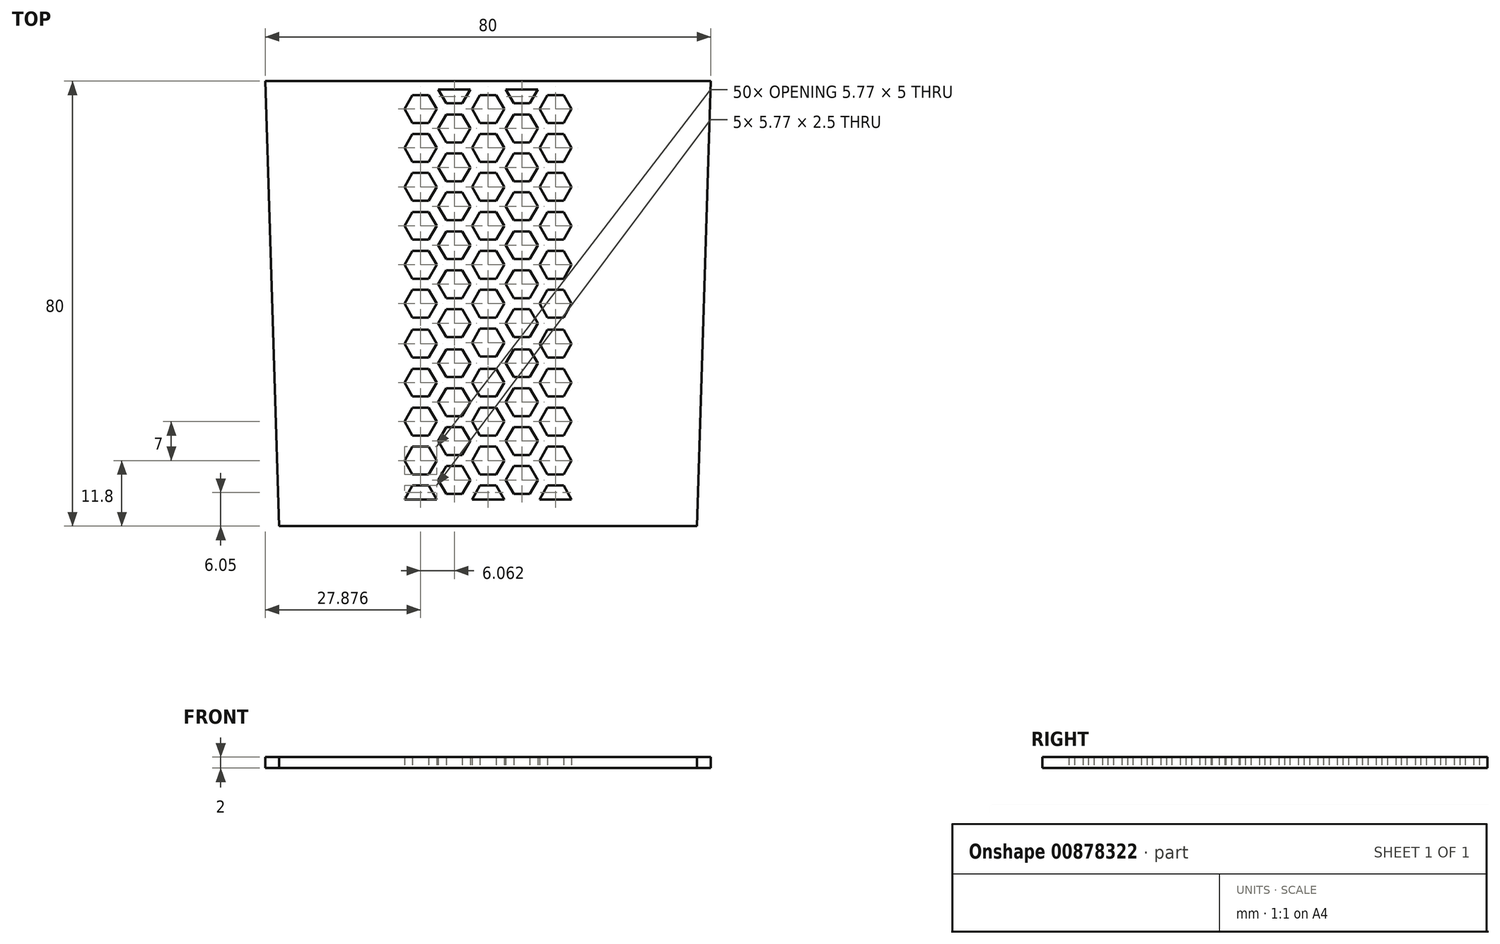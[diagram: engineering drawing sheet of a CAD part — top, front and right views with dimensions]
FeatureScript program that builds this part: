
annotation { "Feature Type Name" : "Feature", "Feature Type Description" : "" }
export const myFeature = defineFeature(function(context is Context, id is Id, definition is map)
    precondition{}
    {
        {
            var Q0;
            Q0=qCreatedBy(makeId("Top.planeOp"),FACE);
            var sketch = newSketch(context, id + "F0", { "sketchPlane" : qUnion([Q0])});
            skLineSegment(sketch, "E0.bottom", {"start": v(37.5, -40) * mm, "end": v(-37.5, -40) * mm});
            skLineSegment(sketch, "E0.top", {"start": v(40, 40) * mm, "end": v(-40, 40) * mm});
            skLineSegment(sketch, "E1", {"start": v(-40, 40) * mm, "end": v(-37.5, -40) * mm});
            skLineSegment(sketch, "E2", {"start": v(40, 40) * mm, "end": v(37.5, -40) * mm});
            skPoint(sketch, "E3.orphan", {"position": v(-40, -40) * mm});
            skPoint(sketch, "E4.orphan", {"position": v(40, -40) * mm});
            skCircle(sketch, "E5.cCircle", {"center": v(0, 0) * mm, "radius": 2.5 * mm, "construction": true});
            skLineSegment(sketch, "E5.0", {"start": v(1.44, -2.5) * mm, "end": v(-1.44, -2.5) * mm});
            skLineSegment(sketch, "E5.1", {"start": v(-1.44, -2.5) * mm, "end": v(-2.89, 0) * mm});
            skLineSegment(sketch, "E5.2", {"start": v(-2.89, 0) * mm, "end": v(-1.44, 2.5) * mm});
            skLineSegment(sketch, "E5.3", {"start": v(-1.44, 2.5) * mm, "end": v(1.44, 2.5) * mm});
            skLineSegment(sketch, "E5.4", {"start": v(1.44, 2.5) * mm, "end": v(2.89, 0) * mm});
            skLineSegment(sketch, "E5.5", {"start": v(2.89, 0) * mm, "end": v(1.44, -2.5) * mm});
            skPoint(sketch, "E5.0.midPoint", {"position": v(0, -2.5) * mm});
            skCircle(sketch, "E6.cCircle", {"center": v(6.06, -3.5) * mm, "radius": 2.5 * mm, "construction": true});
            skLineSegment(sketch, "E6.0", {"start": v(7.5, -6) * mm, "end": v(4.62, -6) * mm});
            skLineSegment(sketch, "E6.1", {"start": v(4.62, -6) * mm, "end": v(3.18, -3.5) * mm});
            skLineSegment(sketch, "E6.2", {"start": v(3.18, -3.5) * mm, "end": v(4.62, -1) * mm});
            skLineSegment(sketch, "E6.3", {"start": v(4.62, -1) * mm, "end": v(7.5, -1) * mm});
            skLineSegment(sketch, "E6.4", {"start": v(7.5, -1) * mm, "end": v(8.95, -3.5) * mm});
            skLineSegment(sketch, "E6.5", {"start": v(8.95, -3.5) * mm, "end": v(7.5, -6) * mm});
            skPoint(sketch, "E6.0.midPoint", {"position": v(6.06, -6) * mm});
            skCircle(sketch, "E7.cCircle", {"center": v(0, -7) * mm, "radius": 2.5 * mm, "construction": true});
            skLineSegment(sketch, "E7.0", {"start": v(1.44, -9.5) * mm, "end": v(-1.44, -9.5) * mm});
            skLineSegment(sketch, "E7.1", {"start": v(-1.44, -9.5) * mm, "end": v(-2.89, -7) * mm});
            skLineSegment(sketch, "E7.2", {"start": v(-2.89, -7) * mm, "end": v(-1.44, -4.5) * mm});
            skLineSegment(sketch, "E7.3", {"start": v(-1.44, -4.5) * mm, "end": v(1.44, -4.5) * mm});
            skLineSegment(sketch, "E7.4", {"start": v(1.44, -4.5) * mm, "end": v(2.89, -7) * mm});
            skLineSegment(sketch, "E7.5", {"start": v(2.89, -7) * mm, "end": v(1.44, -9.5) * mm});
            skPoint(sketch, "E7.0.midPoint", {"position": v(0, -9.5) * mm});
            skCircle(sketch, "E8.cCircle", {"center": v(-6.06, -3.5) * mm, "radius": 2.5 * mm, "construction": true});
            skLineSegment(sketch, "E8.0", {"start": v(-4.62, -6) * mm, "end": v(-7.5, -6) * mm});
            skLineSegment(sketch, "E8.1", {"start": v(-7.5, -6) * mm, "end": v(-8.95, -3.5) * mm});
            skLineSegment(sketch, "E8.2", {"start": v(-8.95, -3.5) * mm, "end": v(-7.5, -1) * mm});
            skLineSegment(sketch, "E8.3", {"start": v(-7.5, -1) * mm, "end": v(-4.62, -1) * mm});
            skLineSegment(sketch, "E8.4", {"start": v(-4.62, -1) * mm, "end": v(-3.18, -3.5) * mm});
            skLineSegment(sketch, "E8.5", {"start": v(-3.18, -3.5) * mm, "end": v(-4.62, -6) * mm});
            skPoint(sketch, "E8.0.midPoint", {"position": v(-6.06, -6) * mm});
            skCircle(sketch, "E9.cCircle", {"center": v(-12.12, 0) * mm, "radius": 2.5 * mm, "construction": true});
            skLineSegment(sketch, "E9.0", {"start": v(-10.68, -2.5) * mm, "end": v(-13.57, -2.5) * mm});
            skLineSegment(sketch, "E9.1", {"start": v(-13.57, -2.5) * mm, "end": v(-15.01, 0) * mm});
            skLineSegment(sketch, "E9.2", {"start": v(-15.01, 0) * mm, "end": v(-13.57, 2.5) * mm});
            skLineSegment(sketch, "E9.3", {"start": v(-13.57, 2.5) * mm, "end": v(-10.68, 2.5) * mm});
            skLineSegment(sketch, "E9.4", {"start": v(-10.68, 2.5) * mm, "end": v(-9.24, 0) * mm});
            skLineSegment(sketch, "E9.5", {"start": v(-9.24, 0) * mm, "end": v(-10.68, -2.5) * mm});
            skPoint(sketch, "E9.0.midPoint", {"position": v(-12.12, -2.5) * mm});
            skCircle(sketch, "E10.cCircle", {"center": v(-6.06, 3.5) * mm, "radius": 2.5 * mm, "construction": true});
            skLineSegment(sketch, "E10.0", {"start": v(-4.62, 1) * mm, "end": v(-7.5, 1) * mm});
            skLineSegment(sketch, "E10.1", {"start": v(-7.5, 1) * mm, "end": v(-8.95, 3.5) * mm});
            skLineSegment(sketch, "E10.2", {"start": v(-8.95, 3.5) * mm, "end": v(-7.5, 6) * mm});
            skLineSegment(sketch, "E10.3", {"start": v(-7.5, 6) * mm, "end": v(-4.62, 6) * mm});
            skLineSegment(sketch, "E10.4", {"start": v(-4.62, 6) * mm, "end": v(-3.18, 3.5) * mm});
            skLineSegment(sketch, "E10.5", {"start": v(-3.18, 3.5) * mm, "end": v(-4.62, 1) * mm});
            skPoint(sketch, "E10.0.midPoint", {"position": v(-6.06, 1) * mm});
            skCircle(sketch, "E11.cCircle", {"center": v(0, 7) * mm, "radius": 2.5 * mm, "construction": true});
            skLineSegment(sketch, "E11.0", {"start": v(1.44, 4.5) * mm, "end": v(-1.44, 4.5) * mm});
            skLineSegment(sketch, "E11.1", {"start": v(-1.44, 4.5) * mm, "end": v(-2.89, 7) * mm});
            skLineSegment(sketch, "E11.2", {"start": v(-2.89, 7) * mm, "end": v(-1.44, 9.5) * mm});
            skLineSegment(sketch, "E11.3", {"start": v(-1.44, 9.5) * mm, "end": v(1.44, 9.5) * mm});
            skLineSegment(sketch, "E11.4", {"start": v(1.44, 9.5) * mm, "end": v(2.89, 7) * mm});
            skLineSegment(sketch, "E11.5", {"start": v(2.89, 7) * mm, "end": v(1.44, 4.5) * mm});
            skPoint(sketch, "E11.0.midPoint", {"position": v(0, 4.5) * mm});
            skCircle(sketch, "E12.cCircle", {"center": v(6.06, 3.5) * mm, "radius": 2.5 * mm, "construction": true});
            skLineSegment(sketch, "E12.0", {"start": v(7.5, 1) * mm, "end": v(4.62, 1) * mm});
            skLineSegment(sketch, "E12.1", {"start": v(4.62, 1) * mm, "end": v(3.18, 3.5) * mm});
            skLineSegment(sketch, "E12.2", {"start": v(3.18, 3.5) * mm, "end": v(4.62, 6) * mm});
            skLineSegment(sketch, "E12.3", {"start": v(4.62, 6) * mm, "end": v(7.5, 6) * mm});
            skLineSegment(sketch, "E12.4", {"start": v(7.5, 6) * mm, "end": v(8.95, 3.5) * mm});
            skLineSegment(sketch, "E12.5", {"start": v(8.95, 3.5) * mm, "end": v(7.5, 1) * mm});
            skPoint(sketch, "E12.0.midPoint", {"position": v(6.06, 1) * mm});
            skCircle(sketch, "E13.cCircle", {"center": v(12.12, 0) * mm, "radius": 2.5 * mm, "construction": true});
            skLineSegment(sketch, "E13.0", {"start": v(13.57, -2.5) * mm, "end": v(10.68, -2.5) * mm});
            skLineSegment(sketch, "E13.1", {"start": v(10.68, -2.5) * mm, "end": v(9.24, 0) * mm});
            skLineSegment(sketch, "E13.2", {"start": v(9.24, 0) * mm, "end": v(10.68, 2.5) * mm});
            skLineSegment(sketch, "E13.3", {"start": v(10.68, 2.5) * mm, "end": v(13.57, 2.5) * mm});
            skLineSegment(sketch, "E13.4", {"start": v(13.57, 2.5) * mm, "end": v(15.01, 0) * mm});
            skLineSegment(sketch, "E13.5", {"start": v(15.01, 0) * mm, "end": v(13.57, -2.5) * mm});
            skPoint(sketch, "E13.0.midPoint", {"position": v(12.12, -2.5) * mm});
            skCircle(sketch, "E14.cCircle", {"center": v(-12.12, 7) * mm, "radius": 2.5 * mm, "construction": true});
            skLineSegment(sketch, "E14.0", {"start": v(-10.68, 4.5) * mm, "end": v(-13.57, 4.5) * mm});
            skLineSegment(sketch, "E14.1", {"start": v(-13.57, 4.5) * mm, "end": v(-15.01, 7) * mm});
            skLineSegment(sketch, "E14.2", {"start": v(-15.01, 7) * mm, "end": v(-13.57, 9.5) * mm});
            skLineSegment(sketch, "E14.3", {"start": v(-13.57, 9.5) * mm, "end": v(-10.68, 9.5) * mm});
            skLineSegment(sketch, "E14.4", {"start": v(-10.68, 9.5) * mm, "end": v(-9.24, 7) * mm});
            skLineSegment(sketch, "E14.5", {"start": v(-9.24, 7) * mm, "end": v(-10.68, 4.5) * mm});
            skPoint(sketch, "E14.0.midPoint", {"position": v(-12.12, 4.5) * mm});
            skCircle(sketch, "E15.cCircle", {"center": v(-6.06, 10.5) * mm, "radius": 2.5 * mm, "construction": true});
            skLineSegment(sketch, "E15.0", {"start": v(-4.62, 8) * mm, "end": v(-7.5, 8) * mm});
            skLineSegment(sketch, "E15.1", {"start": v(-7.5, 8) * mm, "end": v(-8.95, 10.5) * mm});
            skLineSegment(sketch, "E15.2", {"start": v(-8.95, 10.5) * mm, "end": v(-7.5, 13) * mm});
            skLineSegment(sketch, "E15.3", {"start": v(-7.5, 13) * mm, "end": v(-4.62, 13) * mm});
            skLineSegment(sketch, "E15.4", {"start": v(-4.62, 13) * mm, "end": v(-3.18, 10.5) * mm});
            skLineSegment(sketch, "E15.5", {"start": v(-3.18, 10.5) * mm, "end": v(-4.62, 8) * mm});
            skPoint(sketch, "E15.0.midPoint", {"position": v(-6.06, 8) * mm});
            skCircle(sketch, "E16.cCircle", {"center": v(-12.12, 14) * mm, "radius": 2.5 * mm, "construction": true});
            skLineSegment(sketch, "E16.0", {"start": v(-10.68, 11.5) * mm, "end": v(-13.57, 11.5) * mm});
            skLineSegment(sketch, "E16.1", {"start": v(-13.57, 11.5) * mm, "end": v(-15.01, 14) * mm});
            skLineSegment(sketch, "E16.2", {"start": v(-15.01, 14) * mm, "end": v(-13.57, 16.5) * mm});
            skLineSegment(sketch, "E16.3", {"start": v(-13.57, 16.5) * mm, "end": v(-10.68, 16.5) * mm});
            skLineSegment(sketch, "E16.4", {"start": v(-10.68, 16.5) * mm, "end": v(-9.24, 14) * mm});
            skLineSegment(sketch, "E16.5", {"start": v(-9.24, 14) * mm, "end": v(-10.68, 11.5) * mm});
            skPoint(sketch, "E16.0.midPoint", {"position": v(-12.12, 11.5) * mm});
            skCircle(sketch, "E17.cCircle", {"center": v(6.06, 10.5) * mm, "radius": 2.5 * mm, "construction": true});
            skLineSegment(sketch, "E17.0", {"start": v(7.5, 8) * mm, "end": v(4.62, 8) * mm});
            skLineSegment(sketch, "E17.1", {"start": v(4.62, 8) * mm, "end": v(3.18, 10.5) * mm});
            skLineSegment(sketch, "E17.2", {"start": v(3.18, 10.5) * mm, "end": v(4.62, 13) * mm});
            skLineSegment(sketch, "E17.3", {"start": v(4.62, 13) * mm, "end": v(7.5, 13) * mm});
            skLineSegment(sketch, "E17.4", {"start": v(7.5, 13) * mm, "end": v(8.95, 10.5) * mm});
            skLineSegment(sketch, "E17.5", {"start": v(8.95, 10.5) * mm, "end": v(7.5, 8) * mm});
            skPoint(sketch, "E17.0.midPoint", {"position": v(6.06, 8) * mm});
            skCircle(sketch, "E18.cCircle", {"center": v(12.12, 7) * mm, "radius": 2.5 * mm, "construction": true});
            skLineSegment(sketch, "E18.0", {"start": v(13.57, 4.5) * mm, "end": v(10.68, 4.5) * mm});
            skLineSegment(sketch, "E18.1", {"start": v(10.68, 4.5) * mm, "end": v(9.24, 7) * mm});
            skLineSegment(sketch, "E18.2", {"start": v(9.24, 7) * mm, "end": v(10.68, 9.5) * mm});
            skLineSegment(sketch, "E18.3", {"start": v(10.68, 9.5) * mm, "end": v(13.57, 9.5) * mm});
            skLineSegment(sketch, "E18.4", {"start": v(13.57, 9.5) * mm, "end": v(15.01, 7) * mm});
            skLineSegment(sketch, "E18.5", {"start": v(15.01, 7) * mm, "end": v(13.57, 4.5) * mm});
            skPoint(sketch, "E18.0.midPoint", {"position": v(12.12, 4.5) * mm});
            skCircle(sketch, "E19.cCircle", {"center": v(12.12, 14) * mm, "radius": 2.5 * mm, "construction": true});
            skLineSegment(sketch, "E19.0", {"start": v(13.57, 11.5) * mm, "end": v(10.68, 11.5) * mm});
            skLineSegment(sketch, "E19.1", {"start": v(10.68, 11.5) * mm, "end": v(9.24, 14) * mm});
            skLineSegment(sketch, "E19.2", {"start": v(9.24, 14) * mm, "end": v(10.68, 16.5) * mm});
            skLineSegment(sketch, "E19.3", {"start": v(10.68, 16.5) * mm, "end": v(13.57, 16.5) * mm});
            skLineSegment(sketch, "E19.4", {"start": v(13.57, 16.5) * mm, "end": v(15.01, 14) * mm});
            skLineSegment(sketch, "E19.5", {"start": v(15.01, 14) * mm, "end": v(13.57, 11.5) * mm});
            skPoint(sketch, "E19.0.midPoint", {"position": v(12.12, 11.5) * mm});
            skPoint(sketch, "E20.orphan", {"position": v(24.25, 21) * mm});
            skCircle(sketch, "E21.0.1.0", {"center": v(6.06, 17.5) * mm, "radius": 2.5 * mm, "construction": true});
            skCircle(sketch, "E21.0.1.1", {"center": v(-12.12, 35) * mm, "radius": 2.5 * mm, "construction": true});
            skPoint(sketch, "E21.0.1.2", {"position": v(-6.06, 15) * mm});
            skPoint(sketch, "E21.0.1.3", {"position": v(-12.12, 18.5) * mm});
            skLineSegment(sketch, "E21.0.1.4", {"start": v(-8.95, 24.5) * mm, "end": v(-7.5, 27) * mm});
            skCircle(sketch, "E21.0.1.5", {"center": v(0, 21) * mm, "radius": 2.5 * mm, "construction": true});
            skPoint(sketch, "E21.0.1.6", {"position": v(12.12, 32.5) * mm});
            skPoint(sketch, "E21.0.1.7", {"position": v(-12.12, 25.5) * mm});
            skCircle(sketch, "E21.0.1.8", {"center": v(6.06, 31.5) * mm, "radius": 2.5 * mm, "construction": true});
            skPoint(sketch, "E21.0.1.9", {"position": v(12.12, 18.5) * mm});
            skCircle(sketch, "E21.0.1.10", {"center": v(0, 28) * mm, "radius": 2.5 * mm, "construction": true});
            skLineSegment(sketch, "E21.0.1.11", {"start": v(-15.01, 21) * mm, "end": v(-13.57, 23.5) * mm});
            skCircle(sketch, "E21.0.1.12", {"center": v(-12.12, 28) * mm, "radius": 2.5 * mm, "construction": true});
            skPoint(sketch, "E21.0.1.13", {"position": v(0, 25.5) * mm});
            skPoint(sketch, "E21.0.1.14", {"position": v(-6.06, 22) * mm});
            skPoint(sketch, "E21.0.1.15", {"position": v(-12.12, 32.5) * mm});
            skLineSegment(sketch, "E21.0.1.16", {"start": v(13.57, 30.5) * mm, "end": v(15.01, 28) * mm});
            skPoint(sketch, "E21.0.1.17", {"position": v(0, 18.5) * mm});
            skCircle(sketch, "E21.0.1.18", {"center": v(-6.06, 24.5) * mm, "radius": 2.5 * mm, "construction": true});
            skLineSegment(sketch, "E21.0.1.19", {"start": v(-10.68, 30.5) * mm, "end": v(-9.24, 28) * mm});
            skCircle(sketch, "E21.0.1.20", {"center": v(12.12, 28) * mm, "radius": 2.5 * mm, "construction": true});
            skCircle(sketch, "E21.0.1.21", {"center": v(-6.06, 31.5) * mm, "radius": 2.5 * mm, "construction": true});
            skLineSegment(sketch, "E21.0.1.22", {"start": v(4.62, 29) * mm, "end": v(3.18, 31.5) * mm});
            skCircle(sketch, "E21.0.1.23", {"center": v(6.06, 24.5) * mm, "radius": 2.5 * mm, "construction": true});
            skPoint(sketch, "E21.0.1.24", {"position": v(12.12, 25.5) * mm});
            skPoint(sketch, "E21.0.1.25", {"position": v(-6.06, 29) * mm});
            skCircle(sketch, "E21.0.1.26", {"center": v(-12.12, 21) * mm, "radius": 2.5 * mm, "construction": true});
            skPoint(sketch, "E21.0.1.27", {"position": v(6.06, 15) * mm});
            skCircle(sketch, "E21.0.1.28", {"center": v(-6.06, 17.5) * mm, "radius": 2.5 * mm, "construction": true});
            skPoint(sketch, "E21.0.1.29", {"position": v(6.06, 29) * mm});
            skCircle(sketch, "E21.0.1.30", {"center": v(12.12, 21) * mm, "radius": 2.5 * mm, "construction": true});
            skCircle(sketch, "E21.0.1.31", {"center": v(12.12, 35) * mm, "radius": 2.5 * mm, "construction": true});
            skPoint(sketch, "E21.0.1.32", {"position": v(0, 11.5) * mm});
            skPoint(sketch, "E21.0.1.33", {"position": v(6.06, 22) * mm});
            skCircle(sketch, "E21.0.1.34", {"center": v(0, 14) * mm, "radius": 2.5 * mm, "construction": true});
            skLineSegment(sketch, "E21.0.1.35", {"start": v(-1.44, 23.5) * mm, "end": v(1.44, 23.5) * mm});
            skLineSegment(sketch, "E21.0.1.36", {"start": v(8.95, 31.5) * mm, "end": v(7.5, 29) * mm});
            skLineSegment(sketch, "E21.0.1.37", {"start": v(-8.95, 17.5) * mm, "end": v(-7.5, 20) * mm});
            skLineSegment(sketch, "E21.0.1.38", {"start": v(13.57, 23.5) * mm, "end": v(15.01, 21) * mm});
            skLineSegment(sketch, "E21.0.1.39", {"start": v(1.44, 25.5) * mm, "end": v(-1.44, 25.5) * mm});
            skLineSegment(sketch, "E21.0.1.40", {"start": v(7.5, 29) * mm, "end": v(4.62, 29) * mm});
            skLineSegment(sketch, "E21.0.1.41", {"start": v(-4.62, 20) * mm, "end": v(-3.18, 17.5) * mm});
            skLineSegment(sketch, "E21.0.1.42", {"start": v(-4.62, 15) * mm, "end": v(-7.5, 15) * mm});
            skLineSegment(sketch, "E21.0.1.43", {"start": v(7.5, 20) * mm, "end": v(8.95, 17.5) * mm});
            skLineSegment(sketch, "E21.0.1.44", {"start": v(-4.62, 22) * mm, "end": v(-7.5, 22) * mm});
            skLineSegment(sketch, "E21.0.1.45", {"start": v(-15.01, 35) * mm, "end": v(-13.57, 37.5) * mm});
            skLineSegment(sketch, "E21.0.1.46", {"start": v(-7.5, 22) * mm, "end": v(-8.95, 24.5) * mm});
            skLineSegment(sketch, "E21.0.1.47", {"start": v(3.18, 17.5) * mm, "end": v(4.62, 20) * mm});
            skLineSegment(sketch, "E21.0.1.48", {"start": v(-3.18, 17.5) * mm, "end": v(-4.62, 15) * mm});
            skLineSegment(sketch, "E21.0.1.49", {"start": v(1.44, 18.5) * mm, "end": v(-1.44, 18.5) * mm});
            skLineSegment(sketch, "E21.0.1.50", {"start": v(-4.62, 27) * mm, "end": v(-3.18, 24.5) * mm});
            skLineSegment(sketch, "E21.0.1.51", {"start": v(7.5, 15) * mm, "end": v(4.62, 15) * mm});
            skLineSegment(sketch, "E21.0.1.52", {"start": v(3.18, 24.5) * mm, "end": v(4.62, 27) * mm});
            skLineSegment(sketch, "E21.0.1.53", {"start": v(-7.5, 20) * mm, "end": v(-4.62, 20) * mm});
            skLineSegment(sketch, "E21.0.1.54", {"start": v(-13.57, 37.5) * mm, "end": v(-10.68, 37.5) * mm});
            skLineSegment(sketch, "E21.0.1.55", {"start": v(-13.57, 23.5) * mm, "end": v(-10.68, 23.5) * mm});
            skLineSegment(sketch, "E21.0.1.56", {"start": v(10.68, 37.5) * mm, "end": v(13.57, 37.5) * mm});
            skLineSegment(sketch, "E21.0.1.57", {"start": v(-7.5, 34) * mm, "end": v(-4.62, 34) * mm});
            skLineSegment(sketch, "E21.0.1.58", {"start": v(-9.24, 35) * mm, "end": v(-10.68, 32.5) * mm});
            skLineSegment(sketch, "E21.0.1.59", {"start": v(8.95, 17.5) * mm, "end": v(7.5, 15) * mm});
            skLineSegment(sketch, "E21.0.1.60", {"start": v(9.24, 28) * mm, "end": v(10.68, 30.5) * mm});
            skLineSegment(sketch, "E21.0.1.61", {"start": v(10.68, 23.5) * mm, "end": v(13.57, 23.5) * mm});
            skLineSegment(sketch, "E21.0.1.62", {"start": v(9.24, 35) * mm, "end": v(10.68, 37.5) * mm});
            skLineSegment(sketch, "E21.0.1.63", {"start": v(-10.68, 32.5) * mm, "end": v(-13.57, 32.5) * mm});
            skLineSegment(sketch, "E21.0.1.64", {"start": v(-3.18, 24.5) * mm, "end": v(-4.62, 22) * mm});
            skLineSegment(sketch, "E21.0.1.65", {"start": v(-3.18, 31.5) * mm, "end": v(-4.62, 29) * mm});
            skLineSegment(sketch, "E21.0.1.66", {"start": v(-4.62, 29) * mm, "end": v(-7.5, 29) * mm});
            skLineSegment(sketch, "E21.0.1.67", {"start": v(7.5, 27) * mm, "end": v(8.95, 24.5) * mm});
            skLineSegment(sketch, "E21.0.1.68", {"start": v(7.5, 22) * mm, "end": v(4.62, 22) * mm});
            skLineSegment(sketch, "E21.0.1.69", {"start": v(-10.68, 25.5) * mm, "end": v(-13.57, 25.5) * mm});
            skLineSegment(sketch, "E21.0.1.70", {"start": v(-15.01, 28) * mm, "end": v(-13.57, 30.5) * mm});
            skLineSegment(sketch, "E21.0.1.71", {"start": v(-7.5, 15) * mm, "end": v(-8.95, 17.5) * mm});
            skLineSegment(sketch, "E21.0.1.72", {"start": v(13.57, 37.5) * mm, "end": v(15.01, 35) * mm});
            skLineSegment(sketch, "E21.0.1.73", {"start": v(-7.5, 27) * mm, "end": v(-4.62, 27) * mm});
            skLineSegment(sketch, "E21.0.1.74", {"start": v(4.62, 34) * mm, "end": v(7.5, 34) * mm});
            skLineSegment(sketch, "E21.0.1.75", {"start": v(-2.89, 21) * mm, "end": v(-1.44, 23.5) * mm});
            skLineSegment(sketch, "E21.0.1.76", {"start": v(-13.57, 32.5) * mm, "end": v(-15.01, 35) * mm});
            skLineSegment(sketch, "E21.0.1.77", {"start": v(-10.68, 37.5) * mm, "end": v(-9.24, 35) * mm});
            skLineSegment(sketch, "E21.0.1.78", {"start": v(2.89, 14) * mm, "end": v(1.44, 11.5) * mm});
            skLineSegment(sketch, "E21.0.1.79", {"start": v(15.01, 35) * mm, "end": v(13.57, 32.5) * mm});
            skLineSegment(sketch, "E21.0.1.80", {"start": v(-1.44, 11.5) * mm, "end": v(-2.89, 14) * mm});
            skLineSegment(sketch, "E21.0.1.81", {"start": v(8.95, 24.5) * mm, "end": v(7.5, 22) * mm});
            skLineSegment(sketch, "E21.0.1.82", {"start": v(-13.57, 30.5) * mm, "end": v(-10.68, 30.5) * mm});
            skLineSegment(sketch, "E21.0.1.83", {"start": v(-1.44, 16.5) * mm, "end": v(1.44, 16.5) * mm});
            skLineSegment(sketch, "E21.0.1.84", {"start": v(9.24, 21) * mm, "end": v(10.68, 23.5) * mm});
            skLineSegment(sketch, "E21.0.1.85", {"start": v(1.44, 30.5) * mm, "end": v(2.89, 28) * mm});
            skLineSegment(sketch, "E21.0.1.86", {"start": v(10.68, 32.5) * mm, "end": v(9.24, 35) * mm});
            skLineSegment(sketch, "E21.0.1.87", {"start": v(-10.68, 18.5) * mm, "end": v(-13.57, 18.5) * mm});
            skLineSegment(sketch, "E21.0.1.88", {"start": v(4.62, 22) * mm, "end": v(3.18, 24.5) * mm});
            skLineSegment(sketch, "E21.0.1.89", {"start": v(-10.68, 23.5) * mm, "end": v(-9.24, 21) * mm});
            skLineSegment(sketch, "E21.0.1.90", {"start": v(13.57, 18.5) * mm, "end": v(10.68, 18.5) * mm});
            skLineSegment(sketch, "E21.0.1.91", {"start": v(13.57, 32.5) * mm, "end": v(10.68, 32.5) * mm});
            skLineSegment(sketch, "E21.0.1.92", {"start": v(10.68, 30.5) * mm, "end": v(13.57, 30.5) * mm});
            skLineSegment(sketch, "E21.0.1.93", {"start": v(4.62, 15) * mm, "end": v(3.18, 17.5) * mm});
            skLineSegment(sketch, "E21.0.1.94", {"start": v(4.62, 20) * mm, "end": v(7.5, 20) * mm});
            skLineSegment(sketch, "E21.0.1.95", {"start": v(13.57, 25.5) * mm, "end": v(10.68, 25.5) * mm});
            skLineSegment(sketch, "E21.0.1.96", {"start": v(-2.89, 28) * mm, "end": v(-1.44, 30.5) * mm});
            skLineSegment(sketch, "E21.0.1.97", {"start": v(4.62, 27) * mm, "end": v(7.5, 27) * mm});
            skLineSegment(sketch, "E21.0.1.98", {"start": v(-7.5, 29) * mm, "end": v(-8.95, 31.5) * mm});
            skLineSegment(sketch, "E21.0.1.99", {"start": v(1.44, 23.5) * mm, "end": v(2.89, 21) * mm});
            skLineSegment(sketch, "E21.0.1.100", {"start": v(1.44, 11.5) * mm, "end": v(-1.44, 11.5) * mm});
            skLineSegment(sketch, "E21.0.1.101", {"start": v(-1.44, 30.5) * mm, "end": v(1.44, 30.5) * mm});
            skLineSegment(sketch, "E21.0.1.102", {"start": v(-13.57, 25.5) * mm, "end": v(-15.01, 28) * mm});
            skLineSegment(sketch, "E21.0.1.103", {"start": v(7.5, 34) * mm, "end": v(8.95, 31.5) * mm});
            skLineSegment(sketch, "E21.0.1.104", {"start": v(2.89, 28) * mm, "end": v(1.44, 25.5) * mm});
            skLineSegment(sketch, "E21.0.1.105", {"start": v(15.01, 21) * mm, "end": v(13.57, 18.5) * mm});
            skLineSegment(sketch, "E21.0.1.106", {"start": v(-1.44, 25.5) * mm, "end": v(-2.89, 28) * mm});
            skLineSegment(sketch, "E21.0.1.107", {"start": v(-4.62, 34) * mm, "end": v(-3.18, 31.5) * mm});
            skLineSegment(sketch, "E21.0.1.108", {"start": v(1.44, 16.5) * mm, "end": v(2.89, 14) * mm});
            skLineSegment(sketch, "E21.0.1.109", {"start": v(15.01, 28) * mm, "end": v(13.57, 25.5) * mm});
            skLineSegment(sketch, "E21.0.1.110", {"start": v(10.68, 25.5) * mm, "end": v(9.24, 28) * mm});
            skLineSegment(sketch, "E21.0.1.111", {"start": v(-9.24, 21) * mm, "end": v(-10.68, 18.5) * mm});
            skLineSegment(sketch, "E21.0.1.112", {"start": v(-9.24, 28) * mm, "end": v(-10.68, 25.5) * mm});
            skLineSegment(sketch, "E21.0.1.113", {"start": v(2.89, 21) * mm, "end": v(1.44, 18.5) * mm});
            skLineSegment(sketch, "E21.0.1.114", {"start": v(-1.44, 18.5) * mm, "end": v(-2.89, 21) * mm});
            skLineSegment(sketch, "E21.0.1.115", {"start": v(-8.95, 31.5) * mm, "end": v(-7.5, 34) * mm});
            skLineSegment(sketch, "E21.0.1.116", {"start": v(-2.89, 14) * mm, "end": v(-1.44, 16.5) * mm});
            skLineSegment(sketch, "E21.0.1.117", {"start": v(10.68, 18.5) * mm, "end": v(9.24, 21) * mm});
            skLineSegment(sketch, "E21.0.1.118", {"start": v(-13.57, 18.5) * mm, "end": v(-15.01, 21) * mm});
            skLineSegment(sketch, "E21.0.1.119", {"start": v(3.18, 31.5) * mm, "end": v(4.62, 34) * mm});
            skLineSegment(sketch, "E21.direction1", {"start": v(-13.57, -2.5) * mm, "end": v(11.43, -2.5) * mm, "construction": true});
            skLineSegment(sketch, "E21.direction2", {"start": v(-13.57, -2.5) * mm, "end": v(-13.57, 18.5) * mm, "construction": true});
            skPoint(sketch, "E22.0.1.2", {"position": v(6.06, -20.2) * mm});
            skPoint(sketch, "E22.0.1.3", {"position": v(12.12, -9.7) * mm});
            skPoint(sketch, "E22.0.1.4", {"position": v(-6.06, -20.2) * mm});
            skPoint(sketch, "E22.0.1.10", {"position": v(-6.06, -27.2) * mm});
            skPoint(sketch, "E22.0.1.11", {"position": v(-6.06, -13.2) * mm});
            skPoint(sketch, "E22.0.1.14", {"position": v(6.06, -34.2) * mm});
            skPoint(sketch, "E22.0.1.15", {"position": v(-12.12, -16.7) * mm});
            skPoint(sketch, "E22.0.1.16", {"position": v(-6.06, -34.2) * mm});
            skPoint(sketch, "E22.0.1.17", {"position": v(6.06, -27.2) * mm});
            skPoint(sketch, "E22.0.1.18", {"position": v(-12.12, -9.7) * mm});
            skPoint(sketch, "E22.0.1.19", {"position": v(-12.12, -30.7) * mm});
            skPoint(sketch, "E22.0.1.20", {"position": v(12.12, -23.7) * mm});
            skPoint(sketch, "E22.0.1.21", {"position": v(0, -23.7) * mm});
            skPoint(sketch, "E22.0.1.22", {"position": v(6.06, -13.2) * mm});
            skPoint(sketch, "E22.0.1.24", {"position": v(0, -16.7) * mm});
            skPoint(sketch, "E22.0.1.25", {"position": v(-12.12, -23.7) * mm});
            skPoint(sketch, "E22.0.1.27", {"position": v(12.12, -16.7) * mm});
            skPoint(sketch, "E22.0.1.28", {"position": v(0, -30.7) * mm});
            skPoint(sketch, "E22.0.1.29", {"position": v(12.12, -30.7) * mm});
            skLineSegment(sketch, "E22.0.1.30", {"start": v(-13.57, -44.7) * mm, "end": v(-13.57, -23.7) * mm, "construction": true});
            skCircle(sketch, "E22.0.1.32", {"center": v(-12.12, -14.2) * mm, "radius": 2.5 * mm, "construction": true});
            skCircle(sketch, "E22.0.1.33", {"center": v(0, -35.2) * mm, "radius": 2.5 * mm, "construction": true});
            skLineSegment(sketch, "E22.0.1.34", {"start": v(4.62, -29.2) * mm, "end": v(7.5, -29.2) * mm});
            skLineSegment(sketch, "E22.0.1.35", {"start": v(7.5, -20.2) * mm, "end": v(4.62, -20.2) * mm});
            skLineSegment(sketch, "E22.0.1.36", {"start": v(-1.44, -23.7) * mm, "end": v(-2.89, -21.2) * mm});
            skLineSegment(sketch, "E22.0.1.38", {"start": v(-15.01, -28.2) * mm, "end": v(-13.57, -25.7) * mm});
            skLineSegment(sketch, "E22.0.1.39", {"start": v(-7.5, -20.2) * mm, "end": v(-8.95, -17.7) * mm});
            skLineSegment(sketch, "E22.0.1.40", {"start": v(10.68, -9.7) * mm, "end": v(9.24, -7.2) * mm});
            skLineSegment(sketch, "E22.0.1.41", {"start": v(-7.5, -22.2) * mm, "end": v(-4.62, -22.2) * mm});
            skLineSegment(sketch, "E22.0.1.42", {"start": v(-7.5, -8.2) * mm, "end": v(-4.62, -8.2) * mm});
            skLineSegment(sketch, "E22.0.1.44", {"start": v(-13.57, -16.7) * mm, "end": v(-15.01, -14.2) * mm});
            skLineSegment(sketch, "E22.0.1.45", {"start": v(13.57, -18.7) * mm, "end": v(15.01, -21.2) * mm});
            skLineSegment(sketch, "E22.0.1.46", {"start": v(-4.62, -22.2) * mm, "end": v(-3.18, -24.7) * mm});
            skLineSegment(sketch, "E22.0.1.48", {"start": v(4.62, -20.2) * mm, "end": v(3.18, -17.7) * mm});
            skLineSegment(sketch, "E22.0.1.49", {"start": v(-13.57, -18.7) * mm, "end": v(-10.68, -18.7) * mm});
            skLineSegment(sketch, "E22.0.1.50", {"start": v(-1.44, -16.7) * mm, "end": v(-2.89, -14.2) * mm});
            skLineSegment(sketch, "E22.0.1.51", {"start": v(2.89, -14.2) * mm, "end": v(1.44, -16.7) * mm});
            skLineSegment(sketch, "E22.0.1.53", {"start": v(-2.89, -14.2) * mm, "end": v(-1.44, -11.7) * mm});
            skLineSegment(sketch, "E22.0.1.54", {"start": v(-9.24, -14.2) * mm, "end": v(-10.68, -16.7) * mm});
            skLineSegment(sketch, "E22.0.1.55", {"start": v(-1.44, -30.7) * mm, "end": v(-2.89, -28.2) * mm});
            skLineSegment(sketch, "E22.0.1.56", {"start": v(13.57, -9.7) * mm, "end": v(10.68, -9.7) * mm});
            skCircle(sketch, "E22.0.1.57", {"center": v(0, -21.2) * mm, "radius": 2.5 * mm, "construction": true});
            skLineSegment(sketch, "E22.0.1.63", {"start": v(1.44, -18.7) * mm, "end": v(2.89, -21.2) * mm});
            skLineSegment(sketch, "E22.0.1.64", {"start": v(-15.01, -7.2) * mm, "end": v(-13.57, -4.7) * mm});
            skLineSegment(sketch, "E22.0.1.66", {"start": v(-4.62, -15.2) * mm, "end": v(-3.18, -17.7) * mm});
            skCircle(sketch, "E22.0.1.67", {"center": v(-6.06, -31.7) * mm, "radius": 2.5 * mm, "construction": true});
            skLineSegment(sketch, "E22.0.1.68", {"start": v(10.68, -4.7) * mm, "end": v(13.57, -4.7) * mm});
            skLineSegment(sketch, "E22.0.1.71", {"start": v(-7.5, -29.2) * mm, "end": v(-4.62, -29.2) * mm});
            skLineSegment(sketch, "E22.0.1.74", {"start": v(8.95, -24.7) * mm, "end": v(7.5, -27.2) * mm});
            skLineSegment(sketch, "E22.0.1.75", {"start": v(-9.24, -21.2) * mm, "end": v(-10.68, -23.7) * mm});
            skLineSegment(sketch, "E22.0.1.76", {"start": v(3.18, -17.7) * mm, "end": v(4.62, -15.2) * mm});
            skCircle(sketch, "E22.0.1.78", {"center": v(-6.06, -10.7) * mm, "radius": 2.5 * mm, "construction": true});
            skCircle(sketch, "E22.0.1.79", {"center": v(6.06, -31.7) * mm, "radius": 2.5 * mm, "construction": true});
            skLineSegment(sketch, "E22.0.1.80", {"start": v(7.5, -29.2) * mm, "end": v(8.95, -31.7) * mm});
            skLineSegment(sketch, "E22.0.1.83", {"start": v(4.62, -8.2) * mm, "end": v(7.5, -8.2) * mm});
            skLineSegment(sketch, "E22.0.1.86", {"start": v(3.18, -31.7) * mm, "end": v(4.62, -29.2) * mm});
            skLineSegment(sketch, "E22.0.1.87", {"start": v(-15.01, -21.2) * mm, "end": v(-13.57, -18.7) * mm});
            skLineSegment(sketch, "E22.0.1.88", {"start": v(-10.68, -32.7) * mm, "end": v(-9.24, -35.2) * mm});
            skCircle(sketch, "E22.0.1.89", {"center": v(12.12, -7.2) * mm, "radius": 2.5 * mm, "construction": true});
            skLineSegment(sketch, "E22.0.1.91", {"start": v(-4.62, -13.2) * mm, "end": v(-7.5, -13.2) * mm});
            skLineSegment(sketch, "E22.0.1.92", {"start": v(13.57, -32.7) * mm, "end": v(15.01, -35.2) * mm});
            skCircle(sketch, "E22.0.1.93", {"center": v(6.06, -17.7) * mm, "radius": 2.5 * mm, "construction": true});
            skLineSegment(sketch, "E22.0.1.94", {"start": v(13.57, -25.7) * mm, "end": v(15.01, -28.2) * mm});
            skLineSegment(sketch, "E22.0.1.95", {"start": v(15.01, -21.2) * mm, "end": v(13.57, -23.7) * mm});
            skLineSegment(sketch, "E22.0.1.97", {"start": v(15.01, -14.2) * mm, "end": v(13.57, -16.7) * mm});
            skCircle(sketch, "E22.0.1.100", {"center": v(-6.06, -17.7) * mm, "radius": 2.5 * mm, "construction": true});
            skLineSegment(sketch, "E22.0.1.101", {"start": v(-7.5, -13.2) * mm, "end": v(-8.95, -10.7) * mm});
            skLineSegment(sketch, "E22.0.1.102", {"start": v(-8.95, -24.7) * mm, "end": v(-7.5, -22.2) * mm});
            skLineSegment(sketch, "E22.0.1.103", {"start": v(-10.68, -18.7) * mm, "end": v(-9.24, -21.2) * mm});
            skLineSegment(sketch, "E22.0.1.104", {"start": v(-13.57, -23.7) * mm, "end": v(-15.01, -21.2) * mm});
            skLineSegment(sketch, "E22.0.1.106", {"start": v(7.5, -13.2) * mm, "end": v(4.62, -13.2) * mm});
            skLineSegment(sketch, "E22.0.1.109", {"start": v(-10.68, -4.7) * mm, "end": v(-9.24, -7.2) * mm});
            skLineSegment(sketch, "E22.0.1.110", {"start": v(13.57, -4.7) * mm, "end": v(15.01, -7.2) * mm});
            skLineSegment(sketch, "E22.0.1.113", {"start": v(9.24, -7.2) * mm, "end": v(10.68, -4.7) * mm});
            skLineSegment(sketch, "E22.0.1.114", {"start": v(-8.95, -17.7) * mm, "end": v(-7.5, -15.2) * mm});
            skLineSegment(sketch, "E22.0.1.115", {"start": v(10.68, -18.7) * mm, "end": v(13.57, -18.7) * mm});
            skLineSegment(sketch, "E22.0.1.116", {"start": v(-4.62, -8.2) * mm, "end": v(-3.18, -10.7) * mm});
            skLineSegment(sketch, "E22.0.1.117", {"start": v(-15.01, -14.2) * mm, "end": v(-13.57, -11.7) * mm});
            skLineSegment(sketch, "E22.0.1.118", {"start": v(13.57, -23.7) * mm, "end": v(10.68, -23.7) * mm});
            skLineSegment(sketch, "E22.0.1.120", {"start": v(13.57, -30.7) * mm, "end": v(10.68, -30.7) * mm});
            skLineSegment(sketch, "E22.0.1.121", {"start": v(-2.89, -21.2) * mm, "end": v(-1.44, -18.7) * mm});
            skLineSegment(sketch, "E22.0.1.123", {"start": v(-9.24, -7.2) * mm, "end": v(-10.68, -9.7) * mm});
            skLineSegment(sketch, "E22.0.1.125", {"start": v(9.24, -14.2) * mm, "end": v(10.68, -11.7) * mm});
            skLineSegment(sketch, "E22.0.1.126", {"start": v(-10.68, -9.7) * mm, "end": v(-13.57, -9.7) * mm});
            skLineSegment(sketch, "E22.0.1.127", {"start": v(15.01, -7.2) * mm, "end": v(13.57, -9.7) * mm});
            skLineSegment(sketch, "E22.0.1.128", {"start": v(8.95, -10.7) * mm, "end": v(7.5, -13.2) * mm});
            skLineSegment(sketch, "E22.0.1.129", {"start": v(-7.5, -34.2) * mm, "end": v(-8.95, -31.7) * mm});
            skCircle(sketch, "E22.0.1.130", {"center": v(-12.12, -21.2) * mm, "radius": 2.5 * mm, "construction": true});
            skLineSegment(sketch, "E22.0.1.131", {"start": v(9.24, -28.2) * mm, "end": v(10.68, -25.7) * mm});
            skCircle(sketch, "E22.0.1.132", {"center": v(6.06, -24.7) * mm, "radius": 2.5 * mm, "construction": true});
            skLineSegment(sketch, "E22.0.1.133", {"start": v(7.5, -15.2) * mm, "end": v(8.95, -17.7) * mm});
            skCircle(sketch, "E22.0.1.135", {"center": v(-12.12, -7.2) * mm, "radius": 2.5 * mm, "construction": true});
            skLineSegment(sketch, "E22.0.1.136", {"start": v(4.62, -27.2) * mm, "end": v(3.18, -24.7) * mm});
            skLineSegment(sketch, "E22.0.1.137", {"start": v(-1.44, -18.7) * mm, "end": v(1.44, -18.7) * mm});
            skLineSegment(sketch, "E22.0.1.139", {"start": v(10.68, -23.7) * mm, "end": v(9.24, -21.2) * mm});
            skLineSegment(sketch, "E22.0.1.140", {"start": v(3.18, -10.7) * mm, "end": v(4.62, -8.2) * mm});
            skLineSegment(sketch, "E22.0.1.141", {"start": v(-15.01, -35.2) * mm, "end": v(-13.57, -32.7) * mm});
            skLineSegment(sketch, "E22.0.1.142", {"start": v(-3.18, -17.7) * mm, "end": v(-4.62, -20.2) * mm});
            skLineSegment(sketch, "E22.0.1.143", {"start": v(7.5, -22.2) * mm, "end": v(8.95, -24.7) * mm});
            skLineSegment(sketch, "E22.0.1.144", {"start": v(10.68, -30.7) * mm, "end": v(9.24, -28.2) * mm});
            skLineSegment(sketch, "E22.0.1.145", {"start": v(-8.95, -10.7) * mm, "end": v(-7.5, -8.2) * mm});
            skLineSegment(sketch, "E22.0.1.146", {"start": v(10.68, -16.7) * mm, "end": v(9.24, -14.2) * mm});
            skCircle(sketch, "E22.0.1.147", {"center": v(12.12, -14.2) * mm, "radius": 2.5 * mm, "construction": true});
            skLineSegment(sketch, "E22.0.1.148", {"start": v(-3.18, -10.7) * mm, "end": v(-4.62, -13.2) * mm});
            skLineSegment(sketch, "E22.0.1.149", {"start": v(7.5, -8.2) * mm, "end": v(8.95, -10.7) * mm});
            skLineSegment(sketch, "E22.0.1.151", {"start": v(2.89, -21.2) * mm, "end": v(1.44, -23.7) * mm});
            skLineSegment(sketch, "E22.0.1.152", {"start": v(4.62, -22.2) * mm, "end": v(7.5, -22.2) * mm});
            skLineSegment(sketch, "E22.0.1.153", {"start": v(1.44, -16.7) * mm, "end": v(-1.44, -16.7) * mm});
            skLineSegment(sketch, "E22.0.1.154", {"start": v(-10.68, -23.7) * mm, "end": v(-13.57, -23.7) * mm});
            skLineSegment(sketch, "E22.0.1.155", {"start": v(10.68, -32.7) * mm, "end": v(13.57, -32.7) * mm});
            skLineSegment(sketch, "E22.0.1.156", {"start": v(-10.68, -16.7) * mm, "end": v(-13.57, -16.7) * mm});
            skLineSegment(sketch, "E22.0.1.157", {"start": v(-7.5, -27.2) * mm, "end": v(-8.95, -24.7) * mm});
            skCircle(sketch, "E22.0.1.158", {"center": v(0, -28.2) * mm, "radius": 2.5 * mm, "construction": true});
            skLineSegment(sketch, "E22.0.1.159", {"start": v(-3.18, -24.7) * mm, "end": v(-4.62, -27.2) * mm});
            skLineSegment(sketch, "E22.0.1.161", {"start": v(-10.68, -11.7) * mm, "end": v(-9.24, -14.2) * mm});
            skLineSegment(sketch, "E22.0.1.162", {"start": v(-13.57, -9.7) * mm, "end": v(-15.01, -7.2) * mm});
            skLineSegment(sketch, "E22.0.1.165", {"start": v(9.24, -21.2) * mm, "end": v(10.68, -18.7) * mm});
            skLineSegment(sketch, "E22.0.1.166", {"start": v(-3.18, -31.7) * mm, "end": v(-4.62, -34.2) * mm});
            skLineSegment(sketch, "E22.0.1.167", {"start": v(15.01, -28.2) * mm, "end": v(13.57, -30.7) * mm});
            skLineSegment(sketch, "E22.0.1.169", {"start": v(13.57, -11.7) * mm, "end": v(15.01, -14.2) * mm});
            skLineSegment(sketch, "E22.0.1.170", {"start": v(8.95, -17.7) * mm, "end": v(7.5, -20.2) * mm});
            skCircle(sketch, "E22.0.1.171", {"center": v(12.12, -35.2) * mm, "radius": 2.5 * mm, "construction": true});
            skLineSegment(sketch, "E22.0.1.172", {"start": v(10.68, -11.7) * mm, "end": v(13.57, -11.7) * mm});
            skCircle(sketch, "E22.0.1.174", {"center": v(-6.06, -24.7) * mm, "radius": 2.5 * mm, "construction": true});
            skLineSegment(sketch, "E22.0.1.175", {"start": v(-4.62, -29.2) * mm, "end": v(-3.18, -31.7) * mm});
            skLineSegment(sketch, "E22.0.1.176", {"start": v(1.44, -23.7) * mm, "end": v(-1.44, -23.7) * mm});
            skCircle(sketch, "E22.0.1.177", {"center": v(12.12, -28.2) * mm, "radius": 2.5 * mm, "construction": true});
            skLineSegment(sketch, "E22.0.1.178", {"start": v(-4.62, -20.2) * mm, "end": v(-7.5, -20.2) * mm});
            skLineSegment(sketch, "E22.0.1.179", {"start": v(8.95, -31.7) * mm, "end": v(7.5, -34.2) * mm});
            skCircle(sketch, "E22.0.1.181", {"center": v(0, -14.2) * mm, "radius": 2.5 * mm, "construction": true});
            skCircle(sketch, "E22.0.1.182", {"center": v(-12.12, -28.2) * mm, "radius": 2.5 * mm, "construction": true});
            skLineSegment(sketch, "E22.0.1.183", {"start": v(1.44, -25.7) * mm, "end": v(2.89, -28.2) * mm});
            skLineSegment(sketch, "E22.0.1.184", {"start": v(1.44, -32.7) * mm, "end": v(2.89, -35.2) * mm});
            skLineSegment(sketch, "E22.0.1.185", {"start": v(1.44, -11.7) * mm, "end": v(2.89, -14.2) * mm});
            skCircle(sketch, "E22.0.1.189", {"center": v(6.06, -10.7) * mm, "radius": 2.5 * mm, "construction": true});
            skLineSegment(sketch, "E22.0.1.191", {"start": v(1.44, -30.7) * mm, "end": v(-1.44, -30.7) * mm});
            skLineSegment(sketch, "E22.0.1.192", {"start": v(-1.44, -11.7) * mm, "end": v(1.44, -11.7) * mm});
            skLineSegment(sketch, "E22.0.1.193", {"start": v(-2.89, -28.2) * mm, "end": v(-1.44, -25.7) * mm});
            skLineSegment(sketch, "E22.0.1.194", {"start": v(2.89, -28.2) * mm, "end": v(1.44, -30.7) * mm});
            skLineSegment(sketch, "E22.0.1.195", {"start": v(-13.57, -30.7) * mm, "end": v(-15.01, -28.2) * mm});
            skLineSegment(sketch, "E22.0.1.196", {"start": v(4.62, -15.2) * mm, "end": v(7.5, -15.2) * mm});
            skCircle(sketch, "E22.0.1.198", {"center": v(12.12, -21.2) * mm, "radius": 2.5 * mm, "construction": true});
            skLineSegment(sketch, "E22.0.1.199", {"start": v(-10.68, -25.7) * mm, "end": v(-9.24, -28.2) * mm});
            skLineSegment(sketch, "E22.0.1.201", {"start": v(3.18, -24.7) * mm, "end": v(4.62, -22.2) * mm});
            skLineSegment(sketch, "E22.0.1.204", {"start": v(-13.57, -11.7) * mm, "end": v(-10.68, -11.7) * mm});
            skLineSegment(sketch, "E22.0.1.206", {"start": v(-2.89, -35.2) * mm, "end": v(-1.44, -32.7) * mm});
            skLineSegment(sketch, "E22.0.1.208", {"start": v(-1.44, -32.7) * mm, "end": v(1.44, -32.7) * mm});
            skLineSegment(sketch, "E22.0.1.209", {"start": v(-13.57, -25.7) * mm, "end": v(-10.68, -25.7) * mm});
            skLineSegment(sketch, "E22.0.1.210", {"start": v(-10.68, -30.7) * mm, "end": v(-13.57, -30.7) * mm});
            skLineSegment(sketch, "E22.0.1.211", {"start": v(4.62, -34.2) * mm, "end": v(3.18, -31.7) * mm});
            skLineSegment(sketch, "E22.0.1.212", {"start": v(-1.44, -25.7) * mm, "end": v(1.44, -25.7) * mm});
            skLineSegment(sketch, "E22.0.1.213", {"start": v(-9.24, -28.2) * mm, "end": v(-10.68, -30.7) * mm});
            skLineSegment(sketch, "E22.0.1.214", {"start": v(10.68, -25.7) * mm, "end": v(13.57, -25.7) * mm});
            skLineSegment(sketch, "E22.0.1.217", {"start": v(-13.57, -4.7) * mm, "end": v(-10.68, -4.7) * mm});
            skLineSegment(sketch, "E22.0.1.221", {"start": v(4.62, -13.2) * mm, "end": v(3.18, -10.7) * mm});
            skLineSegment(sketch, "E22.0.1.225", {"start": v(7.5, -27.2) * mm, "end": v(4.62, -27.2) * mm});
            skLineSegment(sketch, "E22.0.1.226", {"start": v(-4.62, -27.2) * mm, "end": v(-7.5, -27.2) * mm});
            skLineSegment(sketch, "E22.0.1.228", {"start": v(13.57, -16.7) * mm, "end": v(10.68, -16.7) * mm});
            skLineSegment(sketch, "E22.0.1.229", {"start": v(-7.5, -15.2) * mm, "end": v(-4.62, -15.2) * mm});
            skLineSegment(sketch, "E22.0.1.232", {"start": v(-8.95, -31.7) * mm, "end": v(-7.5, -29.2) * mm});
            skLineSegment(sketch, "E22.0.1.239", {"start": v(9.24, -35.2) * mm, "end": v(10.68, -32.7) * mm});
            skLineSegment(sketch, "E22.0.1.240", {"start": v(-13.57, -32.7) * mm, "end": v(-10.68, -32.7) * mm});
            skLineSegment(sketch, "E22.direction2", {"start": v(-13.57, -2.5) * mm, "end": v(-13.57, -44.7) * mm, "construction": true});
            skLineSegment(sketch, "E23", {"start": v(-15.01, -35.2) * mm, "end": v(-9.24, -35.2) * mm});
            skLineSegment(sketch, "E24", {"start": v(-2.89, -35.2) * mm, "end": v(2.89, -35.2) * mm});
            skLineSegment(sketch, "E25", {"start": v(9.24, -35.2) * mm, "end": v(15.01, -35.2) * mm});
            skLineSegment(sketch, "E26", {"start": v(-7.5, -34.2) * mm, "end": v(-4.62, -34.2) * mm});
            skLineSegment(sketch, "E27", {"start": v(4.62, -34.2) * mm, "end": v(7.5, -34.2) * mm});
            skCircle(sketch, "E28.cCircle", {"center": v(0, 35) * mm, "radius": 2.5 * mm, "construction": true});
            skLineSegment(sketch, "E28.0", {"start": v(1.44, 32.5) * mm, "end": v(-1.44, 32.5) * mm});
            skLineSegment(sketch, "E28.1", {"start": v(-1.44, 32.5) * mm, "end": v(-2.89, 35) * mm});
            skLineSegment(sketch, "E28.2", {"start": v(-2.89, 35) * mm, "end": v(-1.44, 37.5) * mm});
            skLineSegment(sketch, "E28.3", {"start": v(-1.44, 37.5) * mm, "end": v(1.44, 37.5) * mm});
            skLineSegment(sketch, "E28.4", {"start": v(1.44, 37.5) * mm, "end": v(2.89, 35) * mm});
            skLineSegment(sketch, "E28.5", {"start": v(2.89, 35) * mm, "end": v(1.44, 32.5) * mm});
            skPoint(sketch, "E28.0.midPoint", {"position": v(0, 32.5) * mm});
            skArc(sketch, "E29.cCircle", {"start": v(-8.56, 38.5) * mm, "mid": v(-6.7, 36.09) * mm, "end": v(-3.9, 37.25) * mm, "construction": true});
            skLineSegment(sketch, "E29.0", {"start": v(-4.62, 36) * mm, "end": v(-7.5, 36) * mm});
            skLineSegment(sketch, "E29.1", {"start": v(-7.5, 36) * mm, "end": v(-8.95, 38.5) * mm});
            skLineSegment(sketch, "E29.5", {"start": v(-3.18, 38.5) * mm, "end": v(-4.62, 36) * mm});
            skPoint(sketch, "E29.0.midPoint", {"position": v(-6.06, 36) * mm});
            skLineSegment(sketch, "E30", {"start": v(-8.95, 38.5) * mm, "end": v(-3.18, 38.5) * mm});
            skPoint(sketch, "E31.orphan", {"position": v(-4.62, 41) * mm});
            skArc(sketch, "E32.cCircle", {"start": v(3.9, 37.25) * mm, "mid": v(6.7, 36.09) * mm, "end": v(8.56, 38.5) * mm, "construction": true});
            skLineSegment(sketch, "E32.0", {"start": v(7.5, 36) * mm, "end": v(4.62, 36) * mm});
            skLineSegment(sketch, "E32.1", {"start": v(4.62, 36) * mm, "end": v(3.18, 38.5) * mm});
            skLineSegment(sketch, "E32.5", {"start": v(8.95, 38.5) * mm, "end": v(7.5, 36) * mm});
            skPoint(sketch, "E32.0.midPoint", {"position": v(6.06, 36) * mm});
            skLineSegment(sketch, "E33", {"start": v(3.18, 38.5) * mm, "end": v(8.95, 38.5) * mm});
            skPoint(sketch, "E34.orphan", {"position": v(7.5, 41) * mm});
            skPoint(sketch, "E35.orphan", {"position": v(4.62, 41) * mm});
            skSolve(sketch);
        }
        {
            var Q0;
            Q0=makeQuery(id+"F0.imprint","IMPRINT",FACE,{"disambiguationData":[TD([[makeQuery(id+"F0.imprint","IMPRINT",EDGE,{"derivedFrom":sQuery(id+"F0.wireOp",EDGE,"E0.bottom")}),-1.0]])]});
            extrude(context, id + "F1", {"entities" : qUnion([Q0]), "depth" : 2 * mm, "offsetDistance" : 25 * mm});
        }
    });
